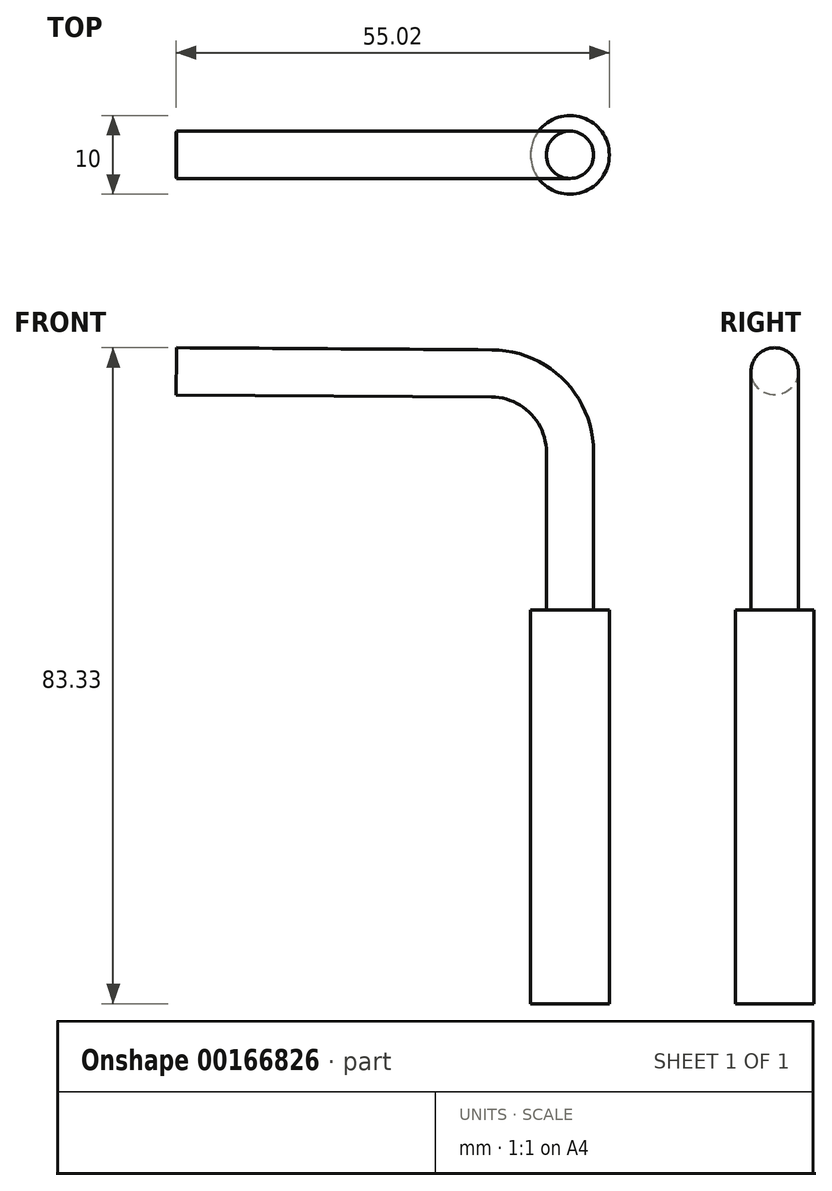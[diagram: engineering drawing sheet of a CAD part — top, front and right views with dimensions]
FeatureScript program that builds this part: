
annotation { "Feature Type Name" : "Feature", "Feature Type Description" : "" }
export const myFeature = defineFeature(function(context is Context, id is Id, definition is map)
    precondition{}
    {
        {
            var Q0;
            Q0=qCreatedBy(makeId("Top.planeOp"),FACE);
            var sketch = newSketch(context, id + "F0", { "sketchPlane" : qUnion([Q0])});
            skCircle(sketch, "E0", {"center": v(0, 0) * mm, "radius": 5 * mm});
            skSolve(sketch);
        }
        {
            var Q0;
            Q0=makeQuery(id+"F0.imprint","IMPRINT",FACE,{"disambiguationData":[TD([[makeQuery(id+"F0.imprint","IMPRINT",EDGE,{"derivedFrom":sQuery(id+"F0.wireOp",EDGE,"E0")}),1.0]])]});
            extrude(context, id + "F1", {"entities" : qUnion([Q0]), "depth" : 50 * mm});
        }
        {
            var Q0;
            Q0=makeQuery(id+"F1.opExtrude","CAP_FACE",FACE,{"disambiguationData":[OSD([sQuery(id+"F0.wireOp",EDGE,"E0")])],"isStart":false});
            var sketch = newSketch(context, id + "F2", { "sketchPlane" : qUnion([Q0])});
            skCircle(sketch, "E1", {"center": v(0, 0) * mm, "radius": 3 * mm});
            skSolve(sketch);
        }
        {
            var Q0;
            Q0=qCreatedBy(makeId("Front.planeOp"),FACE);
            var sketch = newSketch(context, id + "F3", { "sketchPlane" : qUnion([Q0])});
            skLineSegment(sketch, "E2", {"start": v(0, 50) * mm, "end": v(0, 70.07) * mm});
            skLineSegment(sketch, "E3", {"start": v(-9.94, 80.07) * mm, "end": v(-50, 80.33) * mm});
            skPoint(sketch, "E4.visualSharp", {"position": v(0, 80) * mm});
            skArc(sketch, "E4.filletArc", {"start": v(0, 70.07) * mm, "mid": v(-2.9, 77.11) * mm, "end": v(-9.94, 80.07) * mm});
            skSolve(sketch);
        }
        {
            var Q0;
            Q0=makeQuery(id+"F2.imprint","IMPRINT",FACE,{"disambiguationData":[TD([[makeQuery(id+"F2.imprint","IMPRINT",EDGE,{"derivedFrom":sQuery(id+"F2.wireOp",EDGE,"E1")}),1.0]])]});
            var Q1;
            Q1=sQuery(id+"F3.wireOp",EDGE,"E2");
            var Q2;
            Q2=sQuery(id+"F3.wireOp",EDGE,"E4.filletArc");
            var Q3;
            Q3=sQuery(id+"F3.wireOp",EDGE,"E3");
            sweep(context, id + "F4", {"operationType" : NewBodyOperationType.ADD, "profiles" : qUnion([Q0]), "path" : qUnion([Q1, Q2, Q3])});
        }
    });
